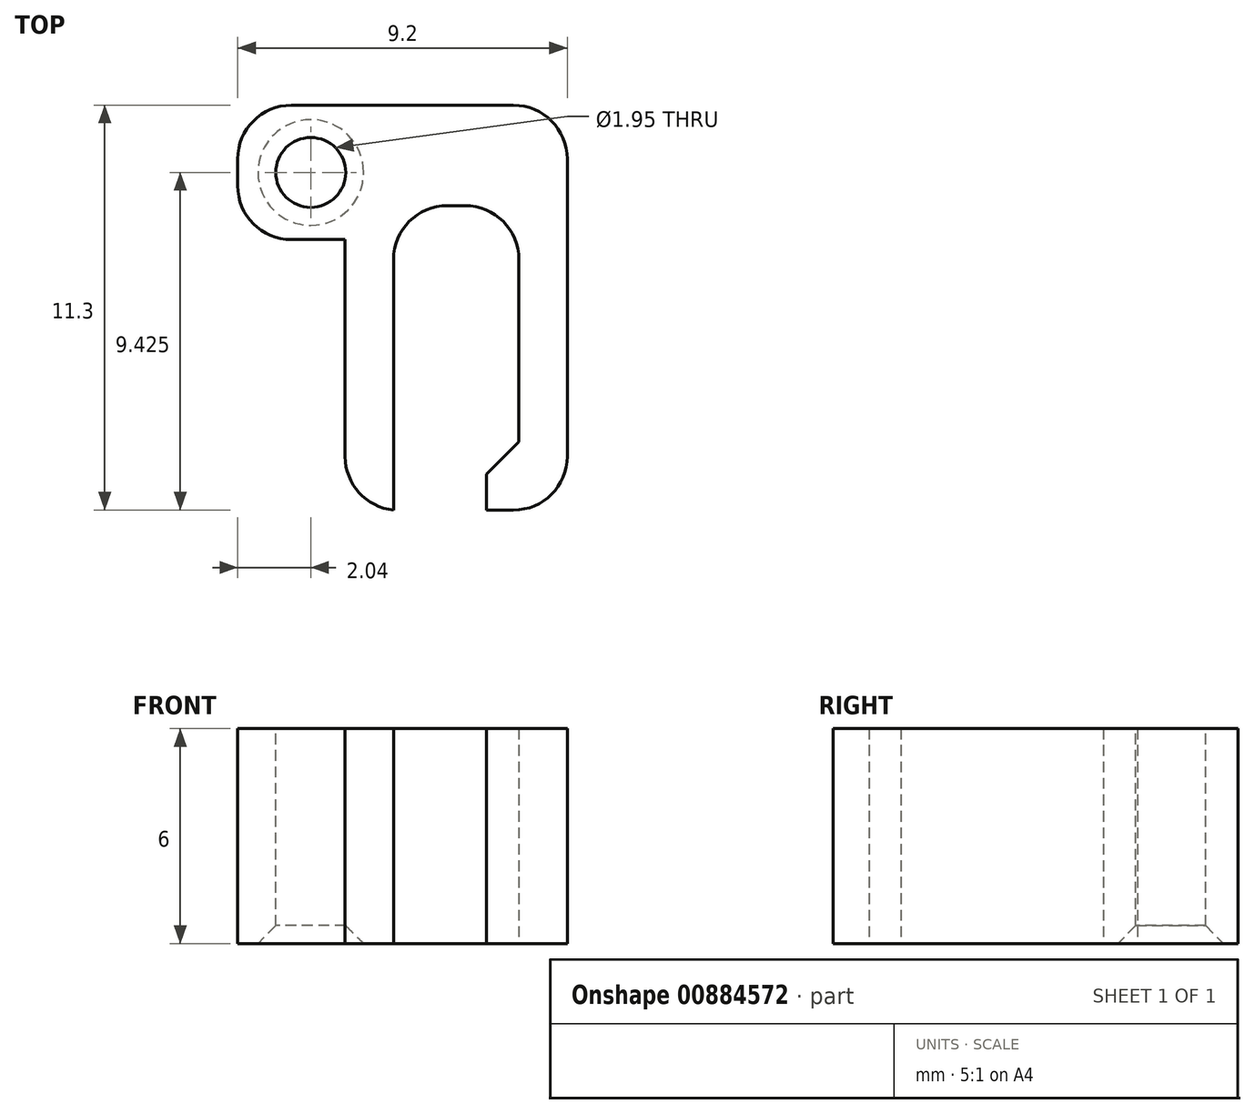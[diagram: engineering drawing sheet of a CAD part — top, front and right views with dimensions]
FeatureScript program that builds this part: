
annotation { "Feature Type Name" : "Feature", "Feature Type Description" : "" }
export const myFeature = defineFeature(function(context is Context, id is Id, definition is map)
    precondition{}
    {
        {
            var Q0;
            Q0=qCreatedBy(makeId("Top.planeOp"),FACE);
            var sketch = newSketch(context, id + "F0", { "sketchPlane" : qUnion([Q0])});
            skLineSegment(sketch, "E0", {"start": v(0, 0) * mm, "end": v(1.35, 0) * mm});
            skLineSegment(sketch, "E1", {"start": v(1.35, 0) * mm, "end": v(1.35, 11.3) * mm});
            skLineSegment(sketch, "E2", {"start": v(1.35, 11.3) * mm, "end": v(-7.85, 11.3) * mm});
            skLineSegment(sketch, "E3", {"start": v(-7.85, 11.3) * mm, "end": v(-7.85, 7.55) * mm});
            skLineSegment(sketch, "E4", {"start": v(-7.85, 7.55) * mm, "end": v(-4.85, 7.55) * mm});
            skLineSegment(sketch, "E5", {"start": v(-4.85, 7.55) * mm, "end": v(-4.85, 0) * mm});
            skLineSegment(sketch, "E6", {"start": v(-4.85, 0) * mm, "end": v(-3.5, 0) * mm});
            skLineSegment(sketch, "E7", {"start": v(-3.5, 0) * mm, "end": v(-3.5, 8.5) * mm});
            skLineSegment(sketch, "E8", {"start": v(-3.5, 8.5) * mm, "end": v(0, 8.5) * mm});
            skLineSegment(sketch, "E9", {"start": v(0, 8.5) * mm, "end": v(0, 0) * mm});
            skLineSegment(sketch, "E10", {"start": v(0, 1.9) * mm, "end": v(-0.9, 1) * mm});
            skLineSegment(sketch, "E11", {"start": v(-0.9, 1) * mm, "end": v(-0.9, 0) * mm});
            skLineSegment(sketch, "E12", {"start": v(-0.9, 0) * mm, "end": v(0, 0) * mm});
            skSolve(sketch);
        }
        {
            var Q0;
            {var subQ3=sQuery(id+"F0.wireOp",EDGE,"E0");Q0=makeQuery(id+"F0.imprint","IMPRINT",FACE,{"disambiguationData":[TD([[makeQuery(id+"F0.imprint","IMPRINT",EDGE,{"derivedFrom":subQ3}),1.0]])]});}
            var Q1;
            {var subQ2=sQuery(id+"F0.wireOp",EDGE,"E10");Q1=makeQuery(id+"F0.imprint","IMPRINT",FACE,{"disambiguationData":[TD([[makeQuery(id+"F0.imprint","IMPRINT",EDGE,{"derivedFrom":subQ2}),1.0]])]});}
            extrude(context, id + "F1", {"entities" : qUnion([Q0, Q1]), "depth" : 6 * mm, "offsetDistance" : 25 * mm});
        }
        {
            var Q0;
            Q0=makeQuery(id+"F1.opExtrude","CAP_FACE",FACE,{"disambiguationData":[OSD([sQuery(id+"F0.wireOp",EDGE,"E0"),sQuery(id+"F0.wireOp",EDGE,"E1"),sQuery(id+"F0.wireOp",EDGE,"E2"),sQuery(id+"F0.wireOp",EDGE,"E3"),sQuery(id+"F0.wireOp",EDGE,"E4"),sQuery(id+"F0.wireOp",EDGE,"E5"),sQuery(id+"F0.wireOp",EDGE,"E6"),sQuery(id+"F0.wireOp",EDGE,"E7"),sQuery(id+"F0.wireOp",EDGE,"E8"),sQuery(id+"F0.wireOp",EDGE,"E9"),sQuery(id+"F0.wireOp",EDGE,"E10"),sQuery(id+"F0.wireOp",EDGE,"E11"),sQuery(id+"F0.wireOp",EDGE,"E12")])],"isStart":false});
            var sketch = newSketch(context, id + "F2", { "sketchPlane" : qUnion([Q0])});
            skCircle(sketch, "E13", {"center": v(-5.8, 9.43) * mm, "radius": 0.97 * mm});
            skLineSegment(sketch, "E14", {"start": v(-7.85, 9.43) * mm, "end": v(-6.8, 9.43) * mm, "construction": true});
            skPoint(sketch, "E15", {"position": v(-7.32, 9.43) * mm});
            skSolve(sketch);
        }
        {
            var Q0;
            {var subQ0=sQuery(id+"F2.wireOp",EDGE,"E13");var subQ1=makeQuery(id+"F1.opExtrude","CAP_EDGE",EDGE,{"disambiguationData":[OSD([sQuery(id+"F0.wireOp",EDGE,"E3")])],"isStart":false});var subQ2=makeQuery(id+"F2.imprint","INTERSECT",VERTEX,{"disambiguationData":[OD(0.0)],"derivedFrom":[subQ1,subQ0]});Q0=makeQuery(id+"F2.imprint","IMPRINT",FACE,{"disambiguationData":[TD([[makeQuery(id+"F2.imprint","IMPRINT",EDGE,{"disambiguationData":[TD([[subQ2,1.0]])],"derivedFrom":subQ0}),1.0]])]});}
            extrude(context, id + "F3", {"entities" : qUnion([Q0]), "operationType" : NewBodyOperationType.REMOVE, "endBound" : BoundingType.THROUGH_ALL, "oppositeDirection" : true, "depth" : 25 * mm, "offsetDistance" : 25 * mm});
        }
        {
            var Q0;
            Q0=makeQuery(id+"F1.opExtrude","SWEPT_EDGE",EDGE,{"disambiguationData":[OSD([sQuery(id+"F0.wireOp",EDGE,"E3"),sQuery(id+"F0.wireOp",EDGE,"E4")])]});
            var Q1;
            Q1=makeQuery(id+"F1.opExtrude","SWEPT_EDGE",EDGE,{"disambiguationData":[OSD([sQuery(id+"F0.wireOp",EDGE,"E2"),sQuery(id+"F0.wireOp",EDGE,"E3")])]});
            var Q2;
            Q2=makeQuery(id+"F1.opExtrude","SWEPT_EDGE",EDGE,{"disambiguationData":[OSD([sQuery(id+"F0.wireOp",EDGE,"E5"),sQuery(id+"F0.wireOp",EDGE,"E6")])]});
            var Q3;
            Q3=makeQuery(id+"F1.opExtrude","SWEPT_EDGE",EDGE,{"disambiguationData":[OSD([sQuery(id+"F0.wireOp",EDGE,"E0"),sQuery(id+"F0.wireOp",EDGE,"E1")])]});
            var Q4;
            Q4=makeQuery(id+"F1.opExtrude","SWEPT_EDGE",EDGE,{"disambiguationData":[OSD([sQuery(id+"F0.wireOp",EDGE,"E1"),sQuery(id+"F0.wireOp",EDGE,"E2")])]});
            var Q5;
            Q5=makeQuery(id+"F1.opExtrude","SWEPT_EDGE",EDGE,{"disambiguationData":[OSD([sQuery(id+"F0.wireOp",EDGE,"E7"),sQuery(id+"F0.wireOp",EDGE,"E8")])]});
            var Q6;
            Q6=makeQuery(id+"F1.opExtrude","SWEPT_EDGE",EDGE,{"disambiguationData":[OSD([sQuery(id+"F0.wireOp",EDGE,"E8"),sQuery(id+"F0.wireOp",EDGE,"E9")])]});
            fillet(context, id + "F4", {"entities" : qUnion([Q0, Q1, Q2, Q3, Q4, Q5, Q6]), "radius" : 1.5 * mm, "tangentPropagation" : true, "allowEdgeOverflow" : false});
        }
        {
            var Q0;
            Q0=makeQuery(id+"F3.boolean.opBoolean","COPY",EDGE,{"derivedFrom":makeQuery(id+"F3.opExtrude","CAP_EDGE",EDGE,{"disambiguationData":[OSD([sQuery(id+"F2.wireOp",EDGE,"E13")])],"isStart":true})});
            var Q1;
            Q1=makeQuery(id+"F3.boolean.opBoolean","INTERSECT",EDGE,{"derivedFrom":[makeQuery(id+"F1.opExtrude","CAP_FACE",FACE,{"disambiguationData":[OSD([sQuery(id+"F0.wireOp",EDGE,"E0"),sQuery(id+"F0.wireOp",EDGE,"E1"),sQuery(id+"F0.wireOp",EDGE,"E2"),sQuery(id+"F0.wireOp",EDGE,"E3"),sQuery(id+"F0.wireOp",EDGE,"E4"),sQuery(id+"F0.wireOp",EDGE,"E5"),sQuery(id+"F0.wireOp",EDGE,"E6"),sQuery(id+"F0.wireOp",EDGE,"E7"),sQuery(id+"F0.wireOp",EDGE,"E8"),sQuery(id+"F0.wireOp",EDGE,"E9"),sQuery(id+"F0.wireOp",EDGE,"E10"),sQuery(id+"F0.wireOp",EDGE,"E11"),sQuery(id+"F0.wireOp",EDGE,"E12")])],"isStart":true}),makeQuery(id+"F3.opExtrude","SWEPT_FACE",FACE,{"disambiguationData":[OSD([sQuery(id+"F2.wireOp",EDGE,"E13")])]})]});
            chamfer(context, id + "F5", {"entities" : qUnion([Q0, Q1]), "width" : 0.5 * mm, "tangentPropagation" : true});
        }
    });
